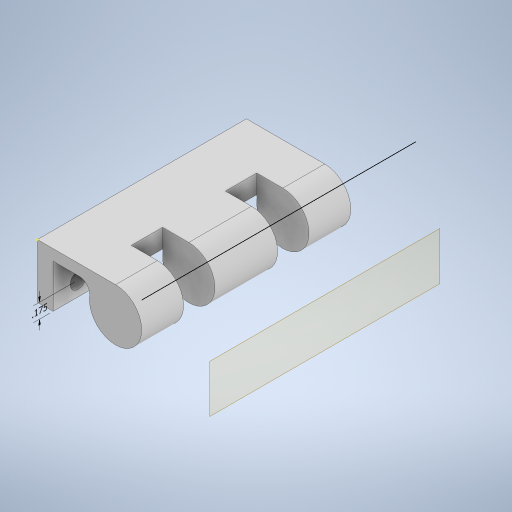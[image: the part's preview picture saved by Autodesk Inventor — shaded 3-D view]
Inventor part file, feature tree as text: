
AUTODESK INVENTOR PART (.ipt)
format: ipt  version: 2024.2 (Build 282272000, 272)  size: 321,536 bytes
history: native  units: in
note: dims shown in document units (in); Inventor stores cm internally (conversion verified against a paired STEP export)
features: sketch x5, extrude x4, other x2, plane x1
ambient origin geometry x8: Origin, YZ Plane, XZ Plane, XY Plane, X Axis, Y Axis, Z Axis, Center Point
bodies: Solid1 (feature_tree)
feature tree (12):
  other  "Annotations"
  extrude  "Extrusion1"  Depth=0.65in
  extrude  "Extrusion2"  Depth=0.3937in
  extrude  "Extrusion3"  Depth=0.13in
  sketch  "Sketch4"  dims[d15=0.04in d16=0.0in d17=0.935in]
  plane  "Work Plane1"
  extrude  "Extrusion4"  Depth=0.935in
  sketch  "Sketch1"  dims[d0=2.5in d1=0.65in]
  sketch  "Sketch2"  dims[d4=2.7559in d6=0.3149in d7=0.3937in d9=1.0in d11=0.3in]
  sketch  "Sketch3"  dims[d12=0.1875in d13=0.0in d14=0.13in]
  sketch  "Sketch6"  dims[d18=0.625in d19=0.125in d20=2.5in d21=0.0in d25=2.0in d26=0.375in d27=0.5in d28=0.375in d29=0.5in d30=0.0in d31=0.0in d32=0.625in d33=0.625in d23=0.0278in d24=0.175in]
  other  "Linear Dimension 1"
